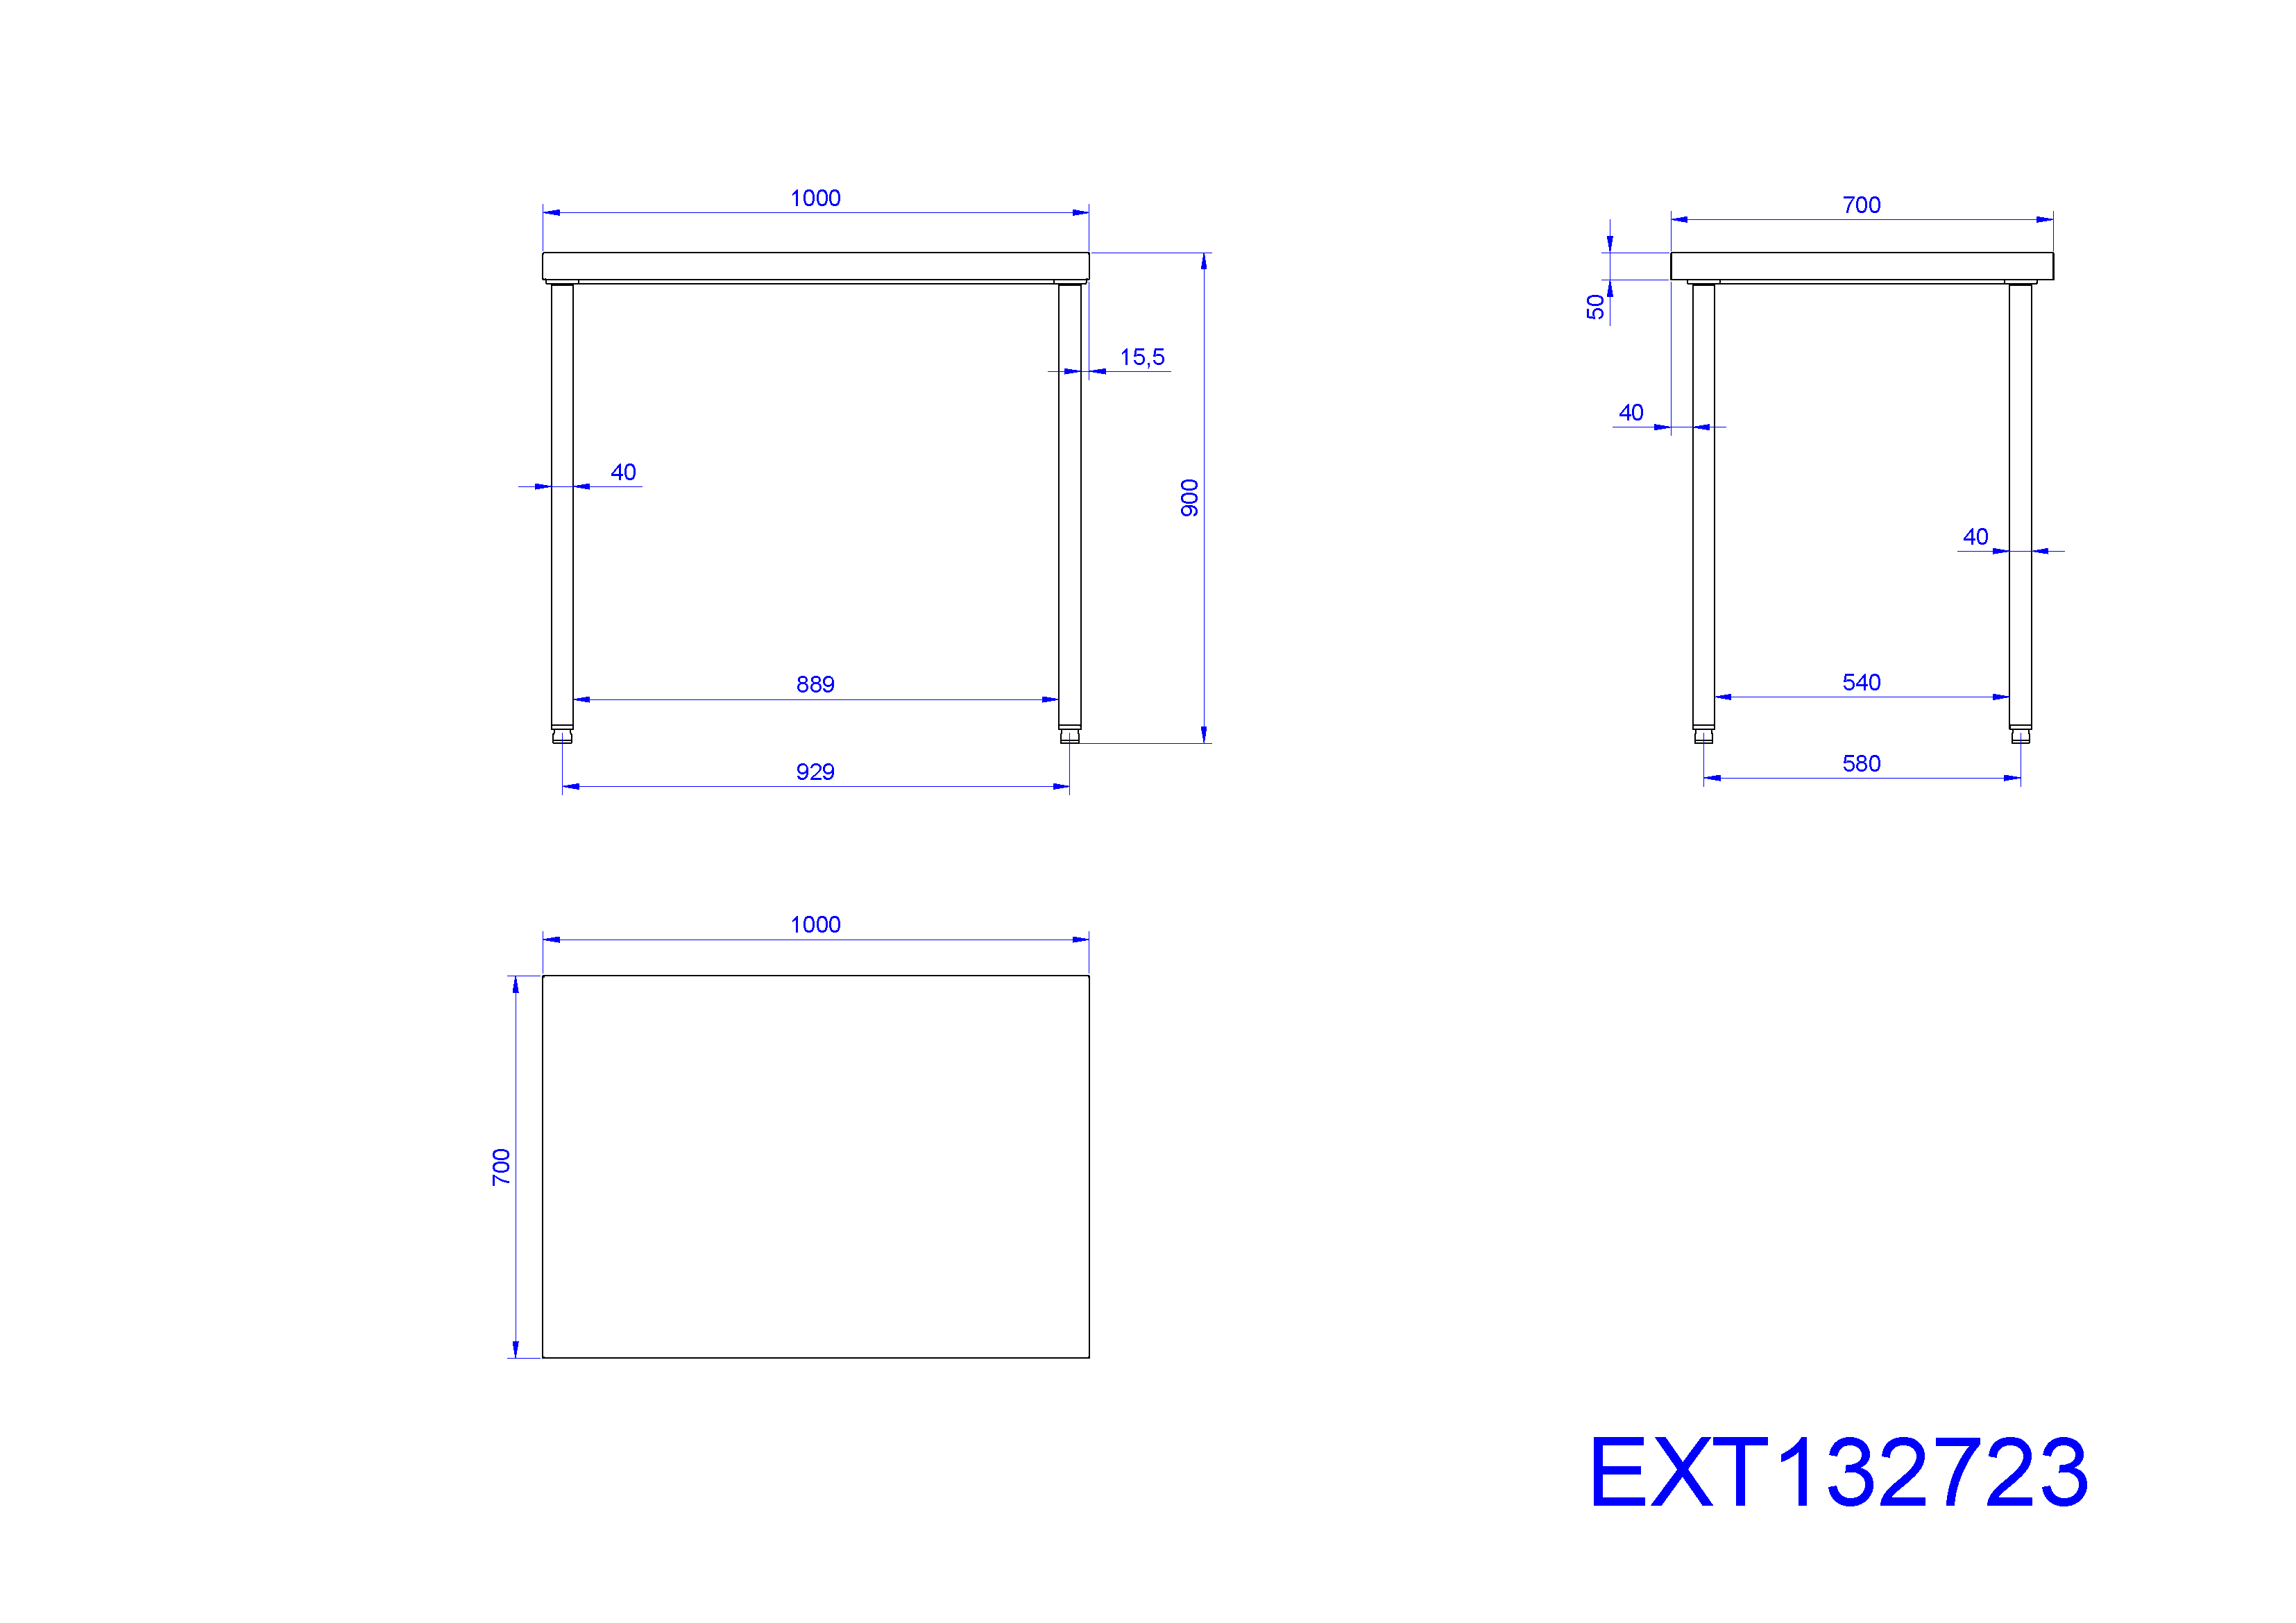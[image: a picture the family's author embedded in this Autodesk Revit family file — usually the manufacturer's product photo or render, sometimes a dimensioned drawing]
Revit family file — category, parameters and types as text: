
# Revit family: QF_ELECTROLUXPROFESSIONAL_132723_TG1000PN
name_source: partatom
category: Attrezzature speciali
units: mm (PartAtom-declared; Revit-internal decimal feet)

## family parameters
Basato su piano di lavoro = No
Condiviso = No
Punto di calcolo locali = No
Quota connettore circolare = Usa diametro
Sempre verticale = Sì
Taglio con vuoti quando caricato = No
Tipo di parte = Normale

## types (1)
- Standard
    Accessory = Sì
    Cold Water Size = 0 mm
    Compressed Air Pressure = 0.0 Pa
    Compressed Air Size = 0 mm
    Compressed Air Volume = 0.0 L/s
    Condensate Return Size = 0 mm
    Cycle = 0 Hz
    Depth Actual = 700 mm  [stored 2.29659 ft]
    Descrizione = WORK TABLE 1000 MM
    Direct Waste Size = 0 mm
    Gas Input Pressure = 0
    Gas KW = 0
    Gas Size = 0 mm
    HP = 0 HP
    Height Actual = 900 mm  [stored 2.95276 ft]
    Hot Water Size = 0 mm
    Item Number = 132723
    Length Actual = 1000 mm  [stored 3.28084 ft]
    Modello = TG1000PN
    Phase = 0
    Produttore = Electrolux Professional
    Prospetto di default = 0 mm  [stored 0 ft]
    Refrigerant Compressor Remote = Sì
    Refrigeration Liquid Line Size = 0 mm  [stored 0 ft]
    Refrigeration Suction Line Size = 0 mm  [stored 0 ft]
    Steam Consumption per Hour = 0
    Steam Supply Maximum Pressure = 0.0 Pa
    Steam Supply Minimum Pressure = 0.0 Pa
    Steam Supply Size = 0 mm
    URL = https://www.electroluxprofessional.com
    URL Manufacturer = https://www.electroluxprofessional.com
    Volts = 0 V
    Watts = 0 W
    Weight = 24.40 kg

note: source unit labels omitted for Gas Input Pressure — the stored unit's dimension contradicts the parameter name (converter mislabeling)

note: [stored X ft] marks values corroborated as IEEE doubles in the binary element streams (Revit-internal decimal feet)

## geometry (parser evidence)
native form markers: Sweep x2
no freeform markers — native parametric forms only
